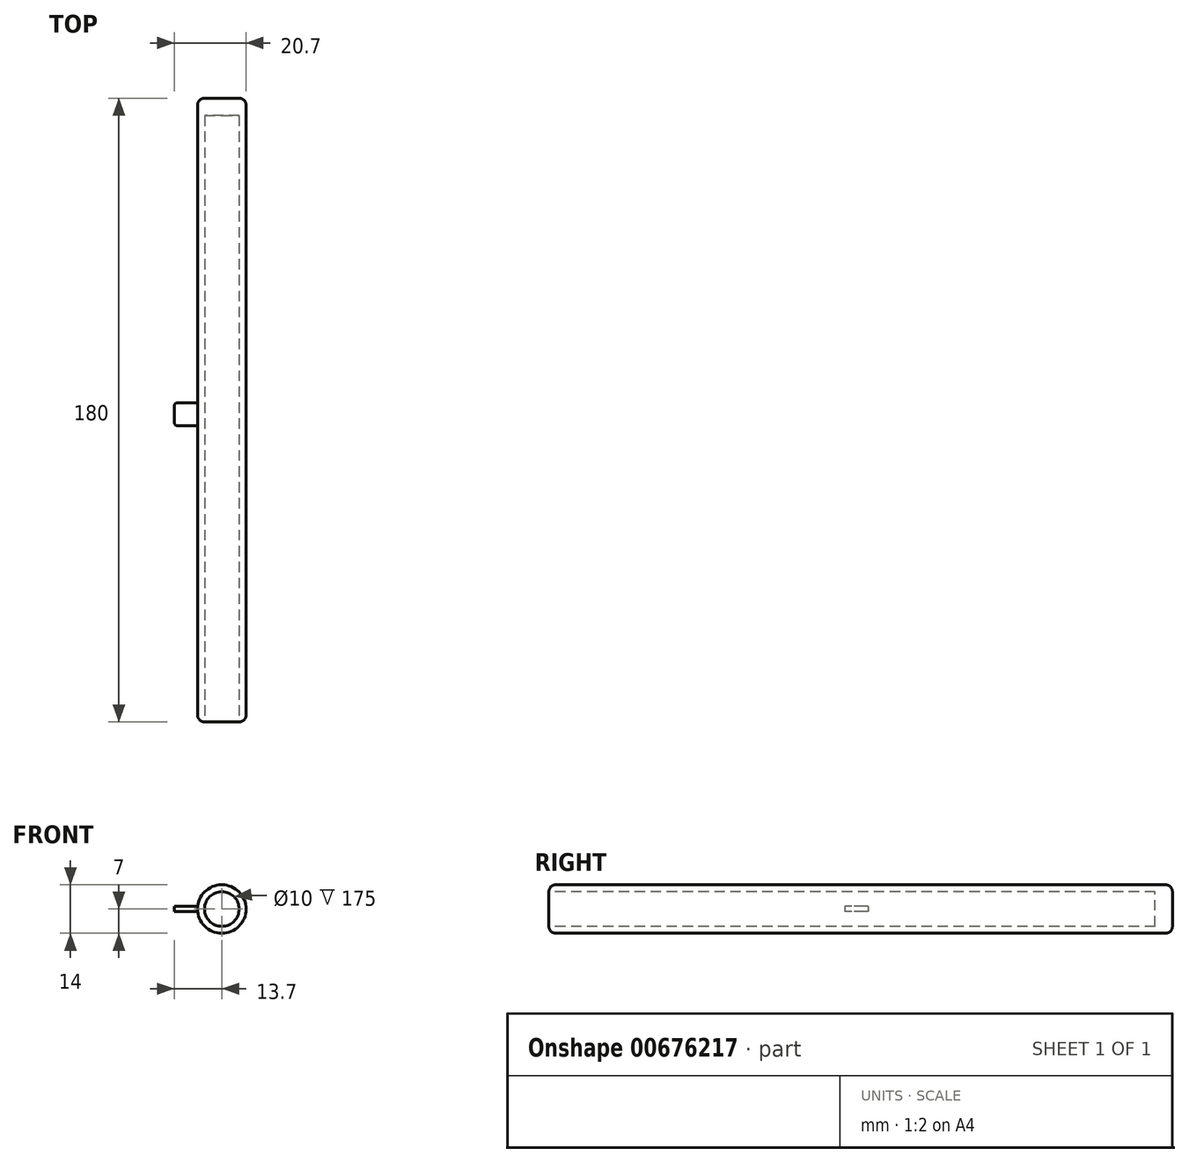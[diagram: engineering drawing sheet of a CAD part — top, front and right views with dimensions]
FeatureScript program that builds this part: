
annotation { "Feature Type Name" : "Feature", "Feature Type Description" : "" }
export const myFeature = defineFeature(function(context is Context, id is Id, definition is map)
    precondition{}
    {
        {
            var Q0;
            Q0=qCreatedBy(makeId("Front.planeOp"),FACE);
            var sketch = newSketch(context, id + "F0", { "sketchPlane" : qUnion([Q0])});
            skCircle(sketch, "E0", {"center": v(0, 0) * mm, "radius": 7 * mm});
            skCircle(sketch, "E1", {"center": v(0, 0) * mm, "radius": 5 * mm});
            skSolve(sketch);
        }
        {
            var Q0;
            Q0=makeQuery(id+"F0.imprint","IMPRINT",FACE,{"disambiguationData":[TD([[makeQuery(id+"F0.imprint","IMPRINT",EDGE,{"derivedFrom":sQuery(id+"F0.wireOp",EDGE,"E0")}),1.0]])]});
            var Q1;
            Q1=makeQuery(id+"F0.imprint","IMPRINT",FACE,{"disambiguationData":[TD([[makeQuery(id+"F0.imprint","IMPRINT",EDGE,{"derivedFrom":sQuery(id+"F0.wireOp",EDGE,"E1")}),1.0]])]});
            extrude(context, id + "F1", {"entities" : qUnion([Q0, Q1]), "endBound" : BoundingType.SYMMETRIC, "depth" : 180 * mm, "offsetDistance" : 25 * mm});
        }
        {
            var Q0;
            Q0=makeQuery(id+"F1.opExtrude","CAP_FACE",FACE,{"disambiguationData":[OSD([sQuery(id+"F0.wireOp",EDGE,"E0")])],"isStart":false});
            var sketch = newSketch(context, id + "F2", { "sketchPlane" : qUnion([Q0])});
            skCircle(sketch, "E2", {"center": v(0, 0) * mm, "radius": 5 * mm});
            skSolve(sketch);
        }
        {
            var Q0;
            Q0=makeQuery(id+"F2.imprint","IMPRINT",FACE,{"disambiguationData":[TD([[makeQuery(id+"F2.imprint","IMPRINT",EDGE,{"derivedFrom":sQuery(id+"F2.wireOp",EDGE,"E2")}),1.0]])]});
            extrude(context, id + "F3", {"entities" : qUnion([Q0]), "operationType" : NewBodyOperationType.REMOVE, "oppositeDirection" : true, "depth" : 175 * mm, "offsetDistance" : 25 * mm});
        }
        {
            var Q0;
            Q0=makeQuery(id+"F1.opExtrude","CAP_EDGE",EDGE,{"disambiguationData":[OSD([sQuery(id+"F0.wireOp",EDGE,"E0")])],"isStart":true});
            var Q1;
            Q1=makeQuery(id+"F1.opExtrude","CAP_EDGE",EDGE,{"disambiguationData":[OSD([sQuery(id+"F0.wireOp",EDGE,"E0")])],"isStart":false});
            fillet(context, id + "F4", {"entities" : qUnion([Q0, Q1]), "radius" : 2 * mm, "tangentPropagation" : true, "allowEdgeOverflow" : false});
        }
        {
            var Q0;
            Q0=qCreatedBy(makeId("Top.planeOp"),FACE);
            var sketch = newSketch(context, id + "F5", { "sketchPlane" : qUnion([Q0])});
            skLineSegment(sketch, "E3.bottom", {"start": v(-7, 2.13) * mm, "end": v(-13.7, 2.13) * mm});
            skLineSegment(sketch, "E3.top", {"start": v(-7, -4.57) * mm, "end": v(-13.7, -4.57) * mm});
            skLineSegment(sketch, "E3.left", {"start": v(-7, 2.13) * mm, "end": v(-7, -4.57) * mm});
            skLineSegment(sketch, "E3.right", {"start": v(-13.7, 2.13) * mm, "end": v(-13.7, -4.57) * mm});
            skLineSegment(sketch, "E4.0", {"start": v(7, 0) * mm, "end": v(-7, 0) * mm});
            skSolve(sketch);
        }
        {
            var Q0;
            {var subQ3=sQuery(id+"F5.wireOp",EDGE,"E3.bottom");Q0=makeQuery(id+"F5.imprint","IMPRINT",FACE,{"disambiguationData":[TD([[makeQuery(id+"F5.imprint","IMPRINT",EDGE,{"derivedFrom":subQ3}),1.0]])]});}
            extrude(context, id + "F6", {"entities" : qUnion([Q0]), "operationType" : NewBodyOperationType.ADD, "endBound" : BoundingType.SYMMETRIC, "depth" : 1.5 * mm, "offsetDistance" : 25 * mm});
        }
        {
            var Q0;
            Q0=makeQuery(id+"F6.opExtrude","SWEPT_EDGE",EDGE,{"disambiguationData":[OSD([sQuery(id+"F5.wireOp",EDGE,"E3.bottom"),sQuery(id+"F5.wireOp",EDGE,"E3.right")])]});
            var Q1;
            Q1=makeQuery(id+"F6.opExtrude","SWEPT_EDGE",EDGE,{"disambiguationData":[OSD([sQuery(id+"F5.wireOp",EDGE,"E3.top"),sQuery(id+"F5.wireOp",EDGE,"E3.right")])]});
            fillet(context, id + "F7", {"entities" : qUnion([Q0, Q1]), "radius" : 1 * mm, "tangentPropagation" : true, "allowEdgeOverflow" : false});
        }
    });
